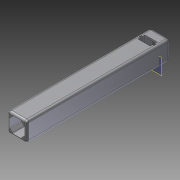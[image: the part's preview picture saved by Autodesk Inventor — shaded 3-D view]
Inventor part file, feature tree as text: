
AUTODESK INVENTOR PART (.ipt)
format: ipt  version: 2012 (Build 160160000, 160)  size: 316,416 bytes
history: native  units: in
note: dims shown in document units (in); Inventor stores cm internally (conversion verified against a paired STEP export)
features: extrude x9, sketch x9, projected_geometry x4, fillet x2, plane x1, reference x1
ambient origin geometry x8: Origin, YZ Plane, XZ Plane, XY Plane, X Axis, Y Axis, Z Axis, Center Point
bodies: Solid1 (feature_tree)
feature tree (26):
  extrude  "Extrusion1"  TaperAngle=135.0deg  [1 undecoded]
  sketch  "Sketch8"  dims[d37=45.0deg d39=0.03in d44=7.874in d45=0.0in d65=0.4331in]
  plane  "Work Plane1"
  extrude  "Extrusion9"  Depth=0.03in
  fillet  "Fillet1"  Radius=7.874in
  fillet  "Fillet2"  Radius=0.4331in
  extrude  "Extrusion14"  Depth=0.2504in
  extrude  "Extrusion15"  Depth=0.0394in
  extrude  "Extrusion16"  Depth=0.0984in
  extrude  "Extrusion17"  Depth=0.0984in
  extrude  "Extrusion18"  Depth=0.1181in
  extrude  "Extrusion19"  Depth=0.3937in TaperAngle=0.0deg
  extrude  "Extrusion20"  Depth=0.3937in TaperAngle=0.0deg
  sketch  "Sketch2"  dims[d21=0.015in d28=135.0deg]
  sketch  "Sketch13"  dims[d66=0.4331in d72=0.2504in]
  sketch  "Sketch14"  dims[d73=0.1969in d74=0.0394in]
  reference  "Reference10"
  sketch  "Sketch15"  dims[d79=0.0984in d80=0.0984in]
  sketch  "Sketch16"  dims[d81=0.0984in d82=0.0984in]
  sketch  "Sketch17"  dims[d85=0.3937in d86=0.0in d97=0.1181in]
  projected_geometry  "Projected Loop3"
  projected_geometry  "Projected Loop4"
  projected_geometry  "Projected Loop5"
  projected_geometry  "Projected Loop6"
  sketch  "Sketch18"  dims[d98=0.1181in d103=0.3937in d104=0.0in]
  sketch  "Sketch19"  dims[d106=0.0118in d107=0.3937in d108=0.0in d109=0.3937in d110=0.0in d111=0.3937in d112=0.1312in d113=0.1312in d114=0.0591in d115=0.0591in d116=0.1312in d117=0.1312in d118=0.3937in d119=0.0in d120=0.3937in d121=0.0in d122=0.3937in d123=0.0in d124=0.1969in d125=0.0in]
note: 1 required parameter value undecoded (feature->parameter linkage not recoverable at this tier; creation-order binding heuristic only, values carry confidence <= 0.55)
